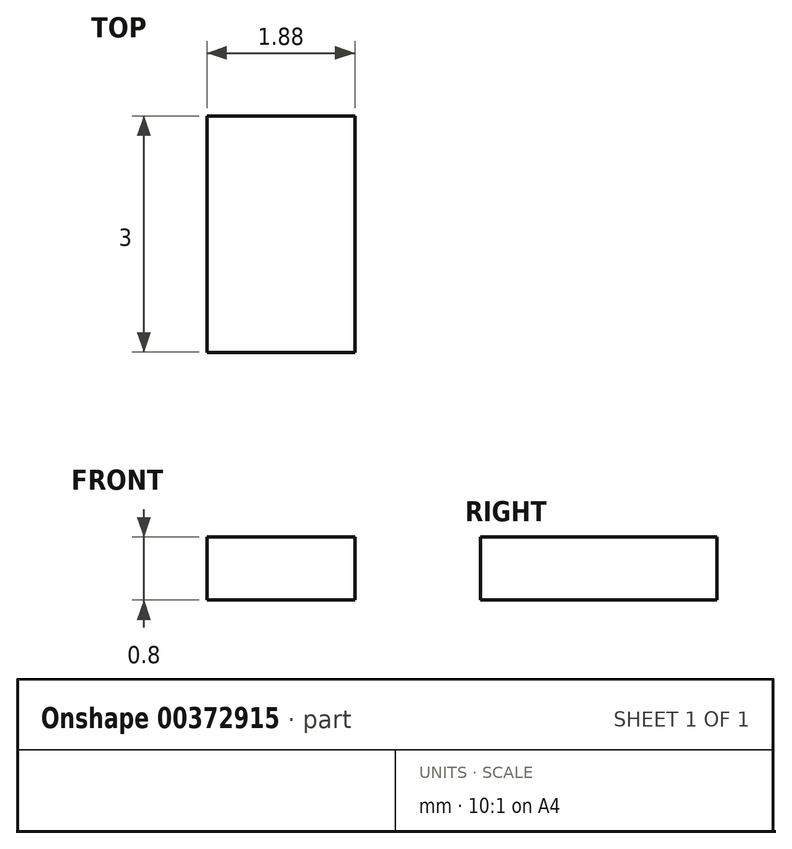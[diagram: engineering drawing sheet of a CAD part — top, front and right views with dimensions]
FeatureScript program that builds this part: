
annotation { "Feature Type Name" : "Feature", "Feature Type Description" : "" }
export const myFeature = defineFeature(function(context is Context, id is Id, definition is map)
    precondition{}
    {
        {
            var Q0;
            Q0=qCreatedBy(makeId("Top.planeOp"),FACE);
            var sketch = newSketch(context, id + "F0", { "sketchPlane" : qUnion([Q0])});
            skLineSegment(sketch, "E0.bottom", {"start": v(-5.73, -4.41) * mm, "end": v(-3.85, -4.41) * mm});
            skLineSegment(sketch, "E0.top", {"start": v(-5.73, -7.41) * mm, "end": v(-3.85, -7.41) * mm});
            skLineSegment(sketch, "E0.left", {"start": v(-5.73, -4.41) * mm, "end": v(-5.73, -7.41) * mm});
            skLineSegment(sketch, "E0.right", {"start": v(-3.85, -4.41) * mm, "end": v(-3.85, -7.41) * mm});
            skSolve(sketch);
        }
        {
            var Q0;
            Q0 = qSketchRegion(id + "F0", true);
            extrude(context, id + "F1", {"entities" : qUnion([Q0]), "depth" : 0.8 * mm});
        }
    });
